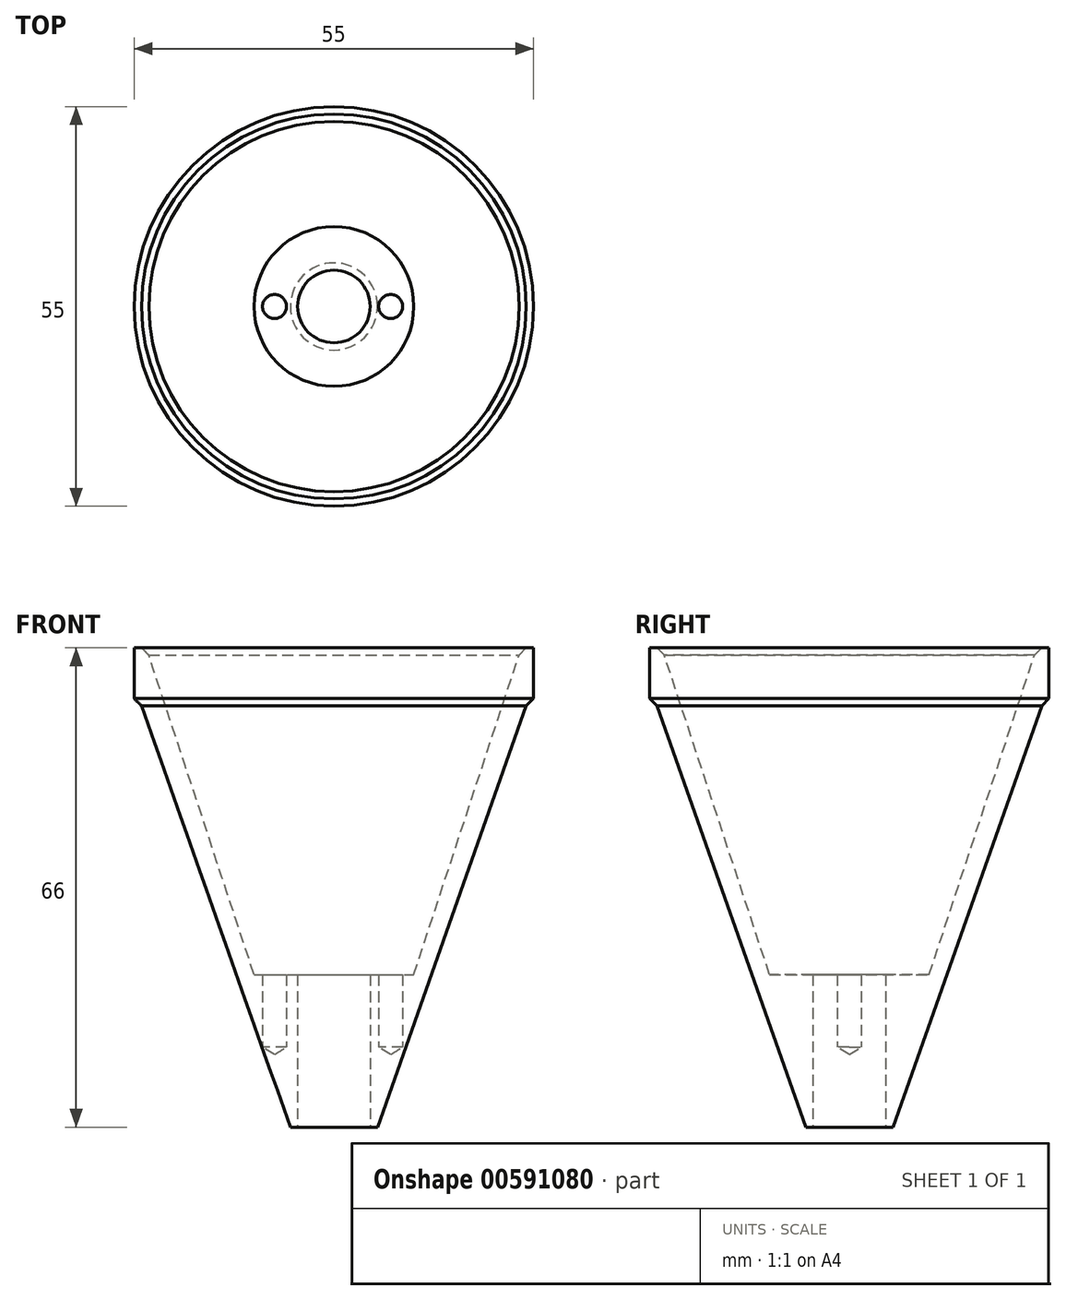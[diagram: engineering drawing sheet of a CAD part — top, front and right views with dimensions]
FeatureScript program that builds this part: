
annotation { "Feature Type Name" : "Feature", "Feature Type Description" : "" }
export const myFeature = defineFeature(function(context is Context, id is Id, definition is map)
    precondition{}
    {
        {
            var Q0;
            Q0=qCreatedBy(makeId("Front.planeOp"),FACE);
            var sketch = newSketch(context, id + "F0", { "sketchPlane" : qUnion([Q0])});
            skLineSegment(sketch, "E0", {"start": v(26.5, 58) * mm, "end": v(6, 0) * mm});
            skLineSegment(sketch, "E1", {"start": v(6, 0) * mm, "end": v(5, 0) * mm});
            skLineSegment(sketch, "E2", {"start": v(5, 0) * mm, "end": v(5, 21) * mm});
            skLineSegment(sketch, "E3", {"start": v(5, 21) * mm, "end": v(11, 21) * mm});
            skLineSegment(sketch, "E4", {"start": v(11, 21) * mm, "end": v(25.5, 65) * mm});
            skLineSegment(sketch, "E5", {"start": v(26.5, 66) * mm, "end": v(27.5, 66) * mm});
            skLineSegment(sketch, "E6", {"start": v(27.5, 66) * mm, "end": v(27.5, 59) * mm});
            skLineSegment(sketch, "E7", {"start": v(26.5, 58) * mm, "end": v(27.5, 59) * mm});
            skLineSegment(sketch, "E8", {"start": v(0, 0) * mm, "end": v(0, 66) * mm});
            skLineSegment(sketch, "E9", {"start": v(26.5, 66) * mm, "end": v(25.5, 65) * mm});
            skSolve(sketch);
        }
        {
            var Q0;
            Q0 = qSketchRegion(id + "F0", true);
            var Q1;
            Q1=sQuery(id+"F0.wireOp",EDGE,"E8");
            revolve(context, id + "F1", {"entities" : qUnion([Q0]), "axis" : qUnion([Q1]), "revolveType" : RevolveType.FULL});
        }
        {
            var Q0;
            Q0=makeQuery(id+"F1.opRevolve","SWEPT_FACE",FACE,{"disambiguationData":[OSD([sQuery(id+"F0.wireOp",EDGE,"E3")])]});
            var sketch = newSketch(context, id + "F2", { "sketchPlane" : qUnion([Q0])});
            skLineSegment(sketch, "E10", {"start": v(-8.18, 0) * mm, "end": v(7.82, 0) * mm});
            skSolve(sketch);
        }
        {
            var Q0;
            Q0=sQuery(id+"F2.wireOp",VERTEX,"E10.start");
            var Q1;
            Q1=sQuery(id+"F2.wireOp",VERTEX,"E10.end");
            var Q2;
            Q2=makeQuery(id+"F1.opRevolve","SWEPT_BODY",BODY,{"disambiguationData":[OSD([sQuery(id+"F0.wireOp",EDGE,"E0"),sQuery(id+"F0.wireOp",EDGE,"E1"),sQuery(id+"F0.wireOp",EDGE,"E2"),sQuery(id+"F0.wireOp",EDGE,"E3"),sQuery(id+"F0.wireOp",EDGE,"E4"),sQuery(id+"F0.wireOp",EDGE,"E5"),sQuery(id+"F0.wireOp",EDGE,"E6"),sQuery(id+"F0.wireOp",EDGE,"E7"),sQuery(id+"F0.wireOp",EDGE,"E9")])]});
            hole(context, id + "F3", {"style" : HoleStyle.SIMPLE, "endStyle" : HoleEndStyle.BLIND, "standardTappedOrClearance" : lookupTablePath({ "standard" : "ISO", "fit" : "Normal", "size" : "M3", "type" : "Clearance" }), "standardBlindInLast" : lookupTablePath({ "fit" : "Standard", "standard" : "ISO", "size" : "M3", "type" : "Clearance" }), "holeDiameter" : 3.3 * mm, "majorDiameter" : 5 * mm, "holeDepth" : 10 * mm, "isTappedThrough" : true, "tappedDepth" : 12 * mm, "tapClearance" : 3, "locations" : qUnion([Q0, Q1]), "scope" : qUnion([Q2])});
        }
    });
